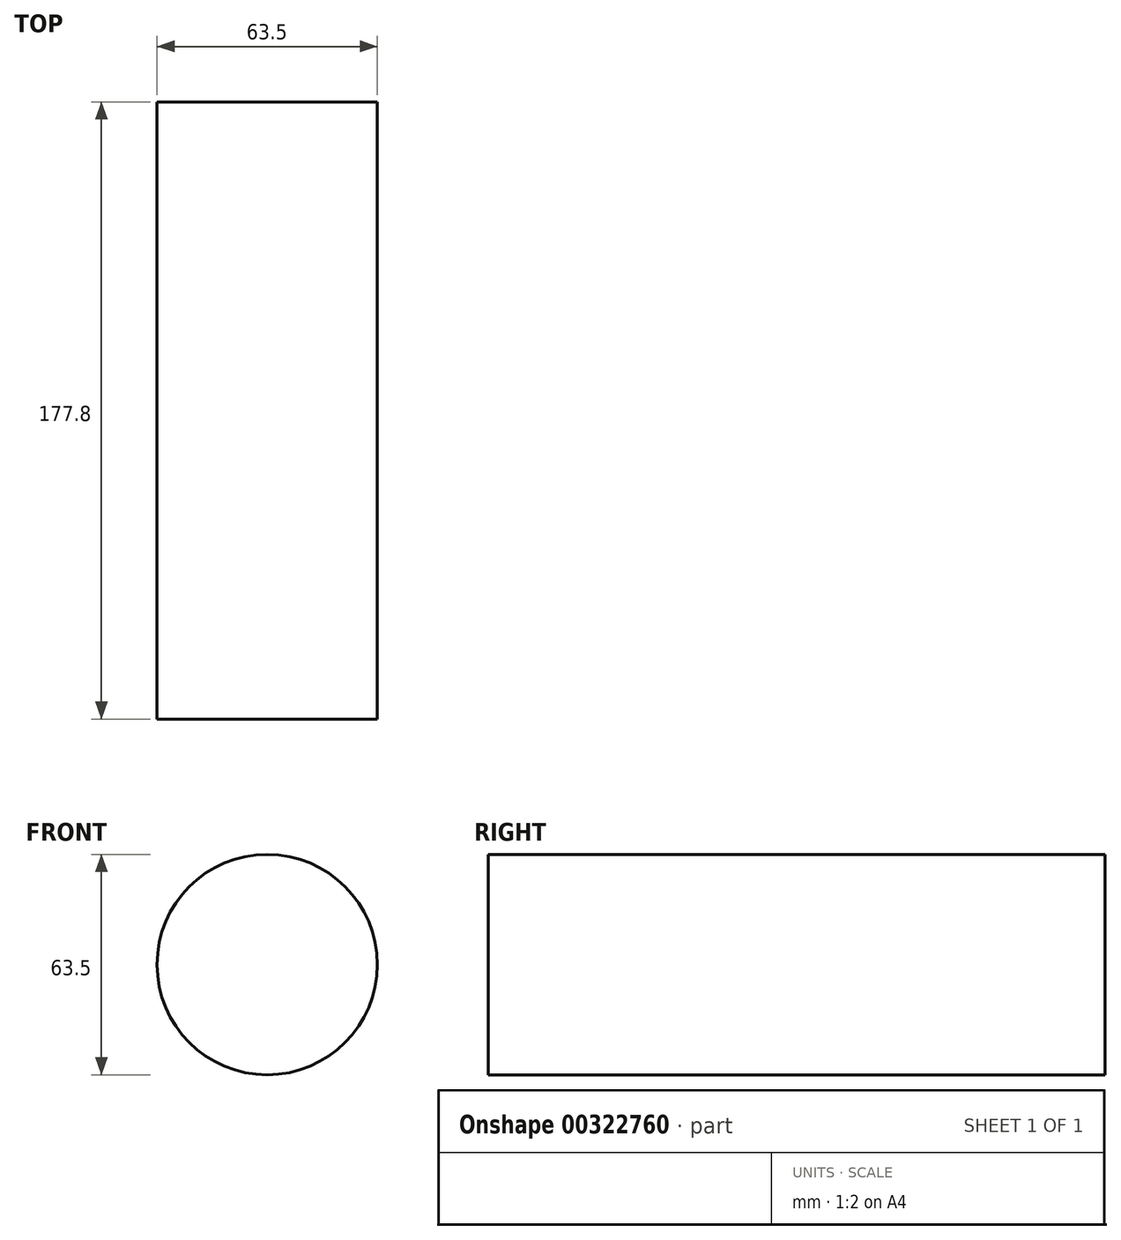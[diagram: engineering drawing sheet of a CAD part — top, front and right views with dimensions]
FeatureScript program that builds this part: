
annotation { "Feature Type Name" : "Feature", "Feature Type Description" : "" }
export const myFeature = defineFeature(function(context is Context, id is Id, definition is map)
    precondition{}
    {
        {
            var Q0;
            Q0=qCreatedBy(makeId("Front.planeOp"),FACE);
            var sketch = newSketch(context, id + "F0", { "sketchPlane" : qUnion([Q0])});
            skCircle(sketch, "E0", {"center": v(0, 0) * mm, "radius": 31.75 * mm});
            skSolve(sketch);
        }
        {
            var Q0;
            Q0 = qSketchRegion(id + "F0", true);
            extrude(context, id + "F1", {"entities" : qUnion([Q0]), "depth" : 177.8 * mm});
        }
    });
